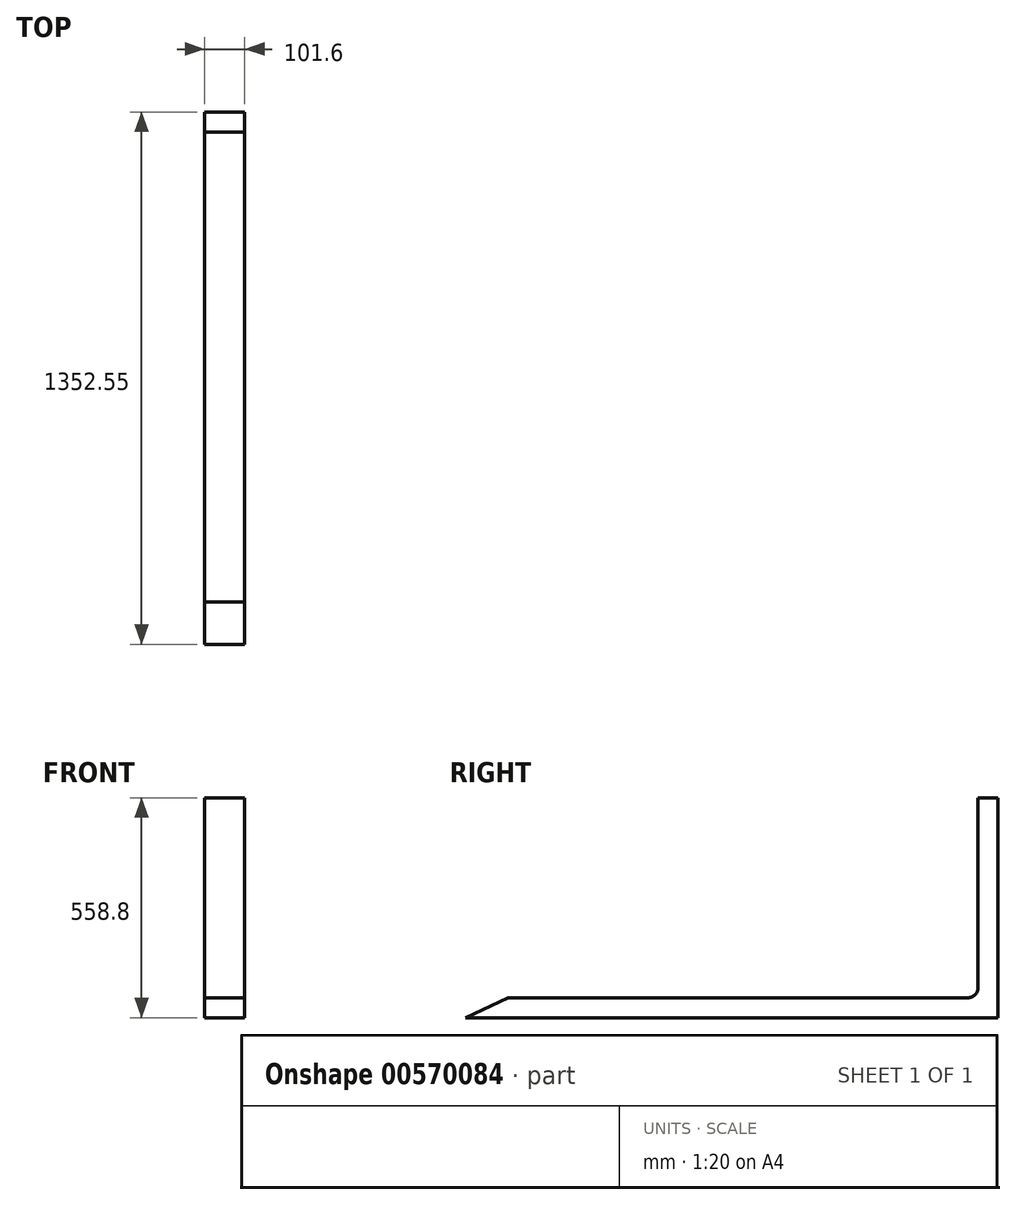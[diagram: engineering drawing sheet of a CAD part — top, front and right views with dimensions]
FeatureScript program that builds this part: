
annotation { "Feature Type Name" : "Feature", "Feature Type Description" : "" }
export const myFeature = defineFeature(function(context is Context, id is Id, definition is map)
    precondition{}
    {
        {
            var Q0;
            Q0=qCreatedBy(makeId("Right.planeOp"),FACE);
            var sketch = newSketch(context, id + "F0", { "sketchPlane" : qUnion([Q0])});
            skLineSegment(sketch, "E0", {"start": v(0, 0) * mm, "end": v(1352.55, 0) * mm});
            skLineSegment(sketch, "E1", {"start": v(0, 0) * mm, "end": v(0, 558.8) * mm});
            skLineSegment(sketch, "E2", {"start": v(0, 558.8) * mm, "end": v(50.8, 558.8) * mm});
            skLineSegment(sketch, "E3", {"start": v(50.8, 558.8) * mm, "end": v(50.8, 50.8) * mm});
            skLineSegment(sketch, "E4", {"start": v(50.8, 50.8) * mm, "end": v(1244.6, 50.8) * mm});
            skLineSegment(sketch, "E5", {"start": v(1244.6, 50.8) * mm, "end": v(1352.55, 0) * mm});
            skLineSegment(sketch, "E6", {"start": v(0, 0) * mm, "end": v(0, 38.1) * mm});
            skSolve(sketch);
        }
        {
            var Q0;
            Q0=makeQuery(id+"F0.imprint","IMPRINT",FACE,{"disambiguationData":[TD([[makeQuery(id+"F0.imprint","IMPRINT",EDGE,{"derivedFrom":sQuery(id+"F0.wireOp",EDGE,"E0")}),1.0]])]});
            extrude(context, id + "F1", {"entities" : qUnion([Q0]), "depth" : 101.6 * mm, "offsetDistance" : 25.4 * mm});
        }
        {
            var Q0;
            Q0=makeQuery(id+"F1.opExtrude","SWEPT_EDGE",EDGE,{"disambiguationData":[OSD([sQuery(id+"F0.wireOp",EDGE,"E0"),sQuery(id+"F0.wireOp",EDGE,"E1")])]});
            fillet(context, id + "F2", {"entities" : qUnion([Q0]), "radius" : 25.4 * mm, "tangentPropagation" : true, "allowEdgeOverflow" : false});
        }
        {
            var Q0;
            Q0=makeQuery(id+"F1.opExtrude","SWEPT_EDGE",EDGE,{"disambiguationData":[OSD([sQuery(id+"F0.wireOp",EDGE,"E3"),sQuery(id+"F0.wireOp",EDGE,"E4")])]});
            fillet(context, id + "F3", {"entities" : qUnion([Q0]), "radius" : 25.4 * mm, "tangentPropagation" : true, "allowEdgeOverflow" : false});
        }
        {
            var Q0;
            Q0 = qSketchRegion(id + "F0", true);
            extrude(context, id + "F4", {"entities" : qUnion([Q0]), "operationType" : NewBodyOperationType.ADD, "depth" : 101.6 * mm, "offsetDistance" : 25.4 * mm});
        }
        {
            var Q0;
            Q0=makeQuery(id+"F1.opExtrude","SWEPT_BODY",BODY,{"disambiguationData":[OSD([sQuery(id+"F0.wireOp",EDGE,"E0"),sQuery(id+"F0.wireOp",EDGE,"E1"),sQuery(id+"F0.wireOp",EDGE,"E2"),sQuery(id+"F0.wireOp",EDGE,"E3"),sQuery(id+"F0.wireOp",EDGE,"E4"),sQuery(id+"F0.wireOp",EDGE,"E5"),sQuery(id+"F0.wireOp",EDGE,"E6"),sQuery(id+"F0.wireOp",EDGE,"wyulNYmT-nDoD-doXk-gOo7-oBcFeDwqtccf")])]});
            var Q1;
            {var subQ0=sQuery(id+"F0.wireOp",EDGE,"E6");Q1=makeQuery(id+"F4.boolean.opBoolean","MERGE",EDGE,{"derivedFrom":[makeQuery(id+"F1.opExtrude","CAP_EDGE",EDGE,{"disambiguationData":[OSD([sQuery(id+"F0.wireOp",EDGE,"E1"),subQ0,sQuery(id+"F0.wireOp",EDGE,"wyulNYmT-nDoD-doXk-gOo7-oBcFeDwqtccf")])],"isStart":false}),makeQuery(id+"F4.opExtrude","CAP_EDGE",EDGE,{"disambiguationData":[OSD([subQ0])],"isStart":false})]});}
            transform(context, id + "F5", {"entities" : qUnion([Q0]), "transformType" : TransformType.ROTATION, "transformAxis" : qUnion([Q1]), "angle" : 180 * degree, "makeCopy" : false});
        }
    });
